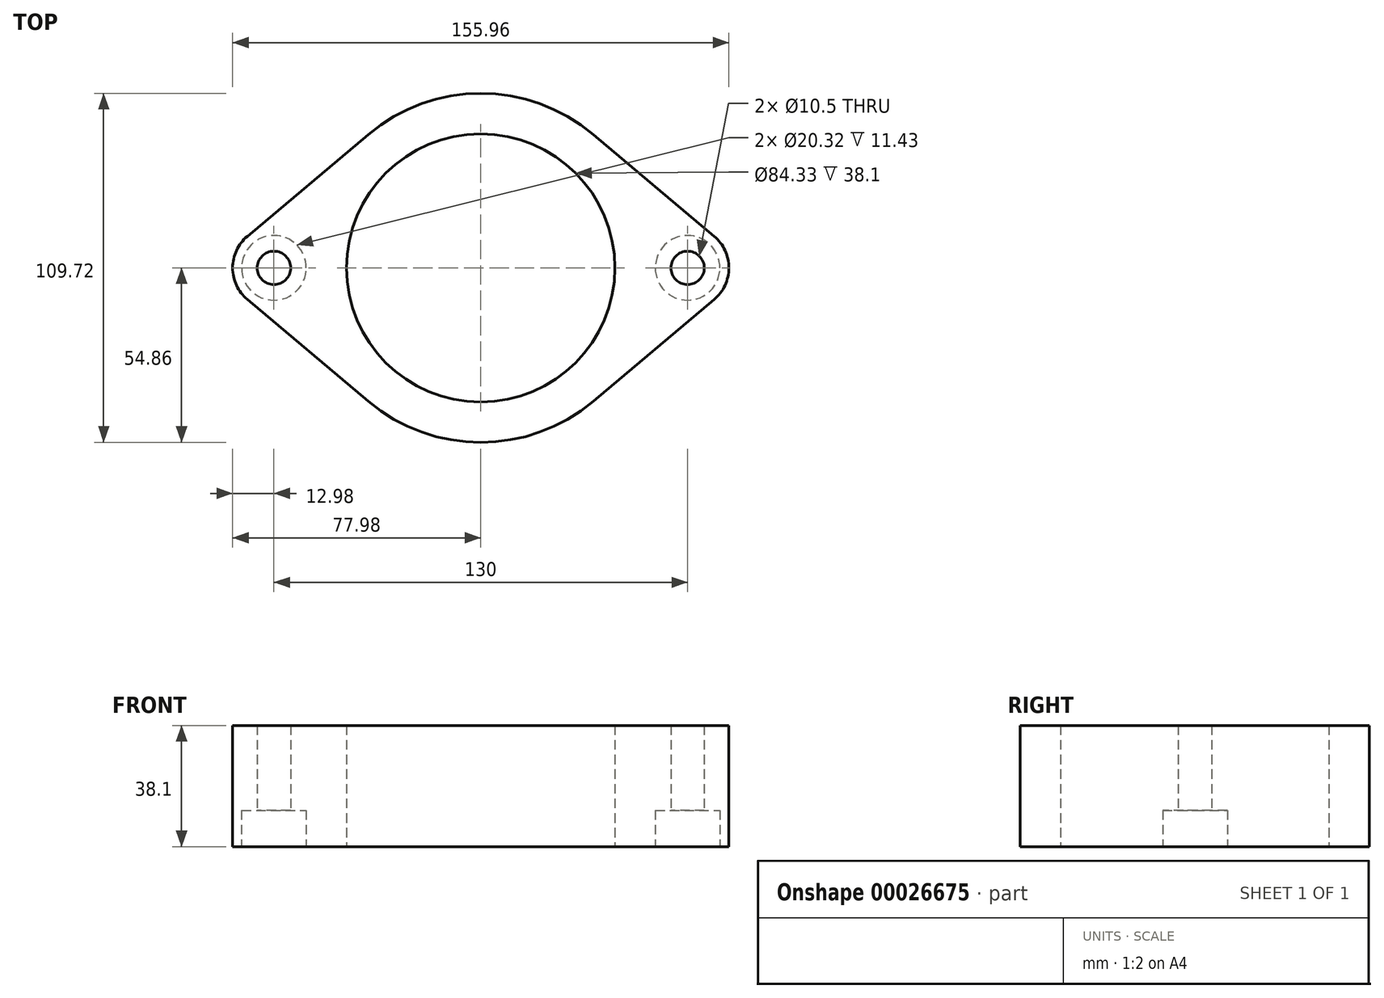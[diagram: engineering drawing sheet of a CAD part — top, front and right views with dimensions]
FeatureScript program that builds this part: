
annotation { "Feature Type Name" : "Feature", "Feature Type Description" : "" }
export const myFeature = defineFeature(function(context is Context, id is Id, definition is map)
    precondition{}
    {
        {
            var Q0;
            Q0=qCreatedBy(makeId("Top.planeOp"),FACE);
            var sketch = newSketch(context, id + "F0", { "sketchPlane" : qUnion([Q0])});
            skLineSegment(sketch, "E0", {"start": v(-65, 0) * mm, "end": v(65, 0) * mm, "construction": true});
            skCircle(sketch, "E1", {"center": v(-65, 0) * mm, "radius": 5.25 * mm});
            skCircle(sketch, "E2", {"center": v(65, 0) * mm, "radius": 5.25 * mm});
            skCircle(sketch, "E3", {"center": v(0, 0) * mm, "radius": 42.16 * mm});
            skArc(sketch, "E4", {"start": v(-73.36, 9.92) * mm, "mid": v(-77.98, 0) * mm, "end": v(-73.36, -9.92) * mm});
            skLineSegment(sketch, "E5", {"start": v(0, -54.86) * mm, "end": v(0, 54.86) * mm, "construction": true});
            skArc(sketch, "E6.MirrorCS", {"start": v(73.36, 9.92) * mm, "mid": v(77.98, 0) * mm, "end": v(73.36, -9.92) * mm});
            skArc(sketch, "E7", {"start": v(35.35, 41.95) * mm, "mid": v(0, 54.86) * mm, "end": v(-35.35, 41.95) * mm});
            skLineSegment(sketch, "E8", {"start": v(-35.35, 41.95) * mm, "end": v(-73.36, 9.92) * mm});
            skLineSegment(sketch, "E9", {"start": v(35.35, 41.95) * mm, "end": v(73.36, 9.92) * mm});
            skLineSegment(sketch, "E10.MirrorCS", {"start": v(-35.35, -41.95) * mm, "end": v(-73.36, -9.92) * mm});
            skArc(sketch, "E11.MirrorCS", {"start": v(35.35, -41.95) * mm, "mid": v(0, -54.86) * mm, "end": v(-35.35, -41.95) * mm});
            skLineSegment(sketch, "E12.MirrorCS", {"start": v(35.35, -41.95) * mm, "end": v(73.36, -9.92) * mm});
            skSolve(sketch);
        }
        {
            var Q0;
            Q0=makeQuery(id+"F0.imprint","IMPRINT",FACE,{"disambiguationData":[TD([[makeQuery(id+"F0.imprint","IMPRINT",EDGE,{"derivedFrom":sQuery(id+"F0.wireOp",EDGE,"E1")}),-1.0]])]});
            extrude(context, id + "F1", {"entities" : qUnion([Q0]), "depth" : 38.1 * mm});
        }
        {
            var Q0;
            Q0=makeQuery(id+"F1.opExtrude","CAP_FACE",FACE,{"disambiguationData":[OSD([sQuery(id+"F0.wireOp",EDGE,"E1"),sQuery(id+"F0.wireOp",EDGE,"E2"),sQuery(id+"F0.wireOp",EDGE,"E3"),sQuery(id+"F0.wireOp",EDGE,"E4"),sQuery(id+"F0.wireOp",EDGE,"E6.MirrorCS"),sQuery(id+"F0.wireOp",EDGE,"E7"),sQuery(id+"F0.wireOp",EDGE,"E8"),sQuery(id+"F0.wireOp",EDGE,"E9"),sQuery(id+"F0.wireOp",EDGE,"E10.MirrorCS"),sQuery(id+"F0.wireOp",EDGE,"E11.MirrorCS"),sQuery(id+"F0.wireOp",EDGE,"E12.MirrorCS")])],"isStart":true});
            var sketch = newSketch(context, id + "F2", { "sketchPlane" : qUnion([Q0])});
            skCircle(sketch, "E13", {"center": v(-65, 0) * mm, "radius": 10.16 * mm});
            skCircle(sketch, "E14", {"center": v(65, 0) * mm, "radius": 10.16 * mm});
            skSolve(sketch);
        }
        {
            var Q0;
            Q0=makeQuery(id+"F2.imprint","IMPRINT",FACE,{"disambiguationData":[TD([[makeQuery(id+"F2.imprint","IMPRINT",EDGE,{"derivedFrom":sQuery(id+"F2.wireOp",EDGE,"E13")}),1.0]])]});
            var Q1;
            Q1=makeQuery(id+"F2.imprint","IMPRINT",FACE,{"disambiguationData":[TD([[makeQuery(id+"F2.imprint","IMPRINT",EDGE,{"derivedFrom":sQuery(id+"F2.wireOp",EDGE,"E14")}),1.0]])]});
            extrude(context, id + "F3", {"entities" : qUnion([Q0, Q1]), "operationType" : NewBodyOperationType.REMOVE, "oppositeDirection" : true, "depth" : 11.43 * mm});
        }
    });
